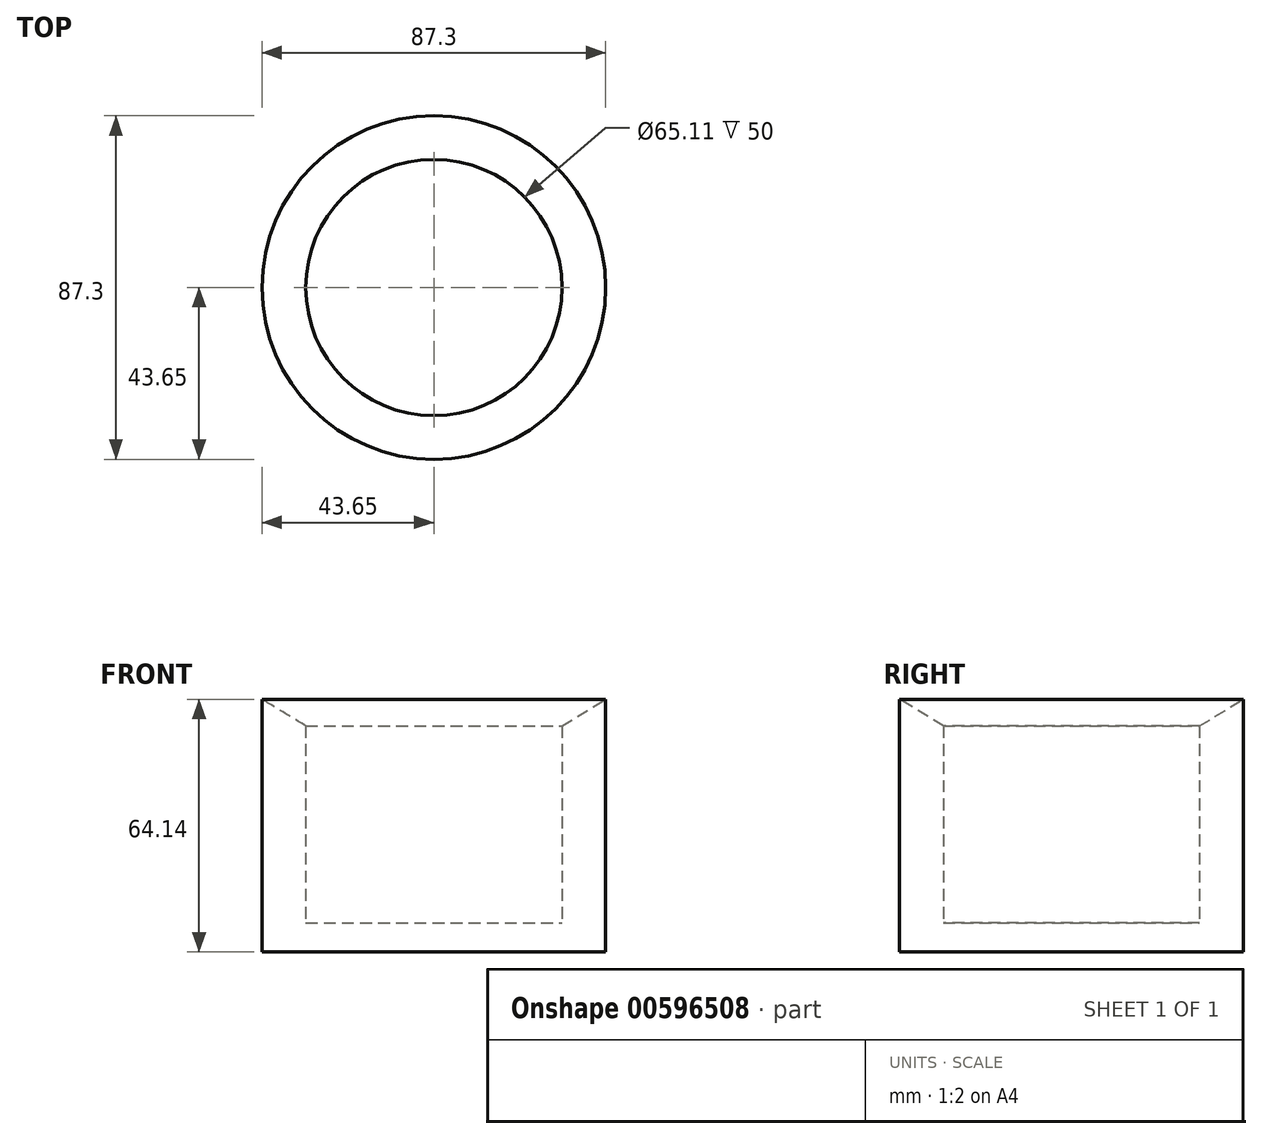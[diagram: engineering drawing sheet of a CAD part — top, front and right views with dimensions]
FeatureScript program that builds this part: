
annotation { "Feature Type Name" : "Feature", "Feature Type Description" : "" }
export const myFeature = defineFeature(function(context is Context, id is Id, definition is map)
    precondition{}
    {
        {
            var Q0;
            Q0=qCreatedBy(makeId("Right.planeOp"),FACE);
            var sketch = newSketch(context, id + "F0", { "sketchPlane" : qUnion([Q0])});
            skLineSegment(sketch, "E0", {"start": v(-43.65, 48.63) * mm, "end": v(-43.65, -15.51) * mm});
            skLineSegment(sketch, "E1", {"start": v(-43.65, -15.51) * mm, "end": v(0, -15.51) * mm});
            skLineSegment(sketch, "E2", {"start": v(0, -15.51) * mm, "end": v(0, -8.12) * mm});
            skLineSegment(sketch, "E3", {"start": v(0, -8.12) * mm, "end": v(-32.56, -8.12) * mm});
            skLineSegment(sketch, "E4", {"start": v(-32.56, -8.12) * mm, "end": v(-32.56, 41.88) * mm});
            skLineSegment(sketch, "E5", {"start": v(-32.56, 41.88) * mm, "end": v(-43.65, 48.63) * mm});
            skSolve(sketch);
        }
        {
            var Q0;
            Q0=makeQuery(id+"F0.imprint","IMPRINT",FACE,{"disambiguationData":[TD([[makeQuery(id+"F0.imprint","IMPRINT",EDGE,{"derivedFrom":sQuery(id+"F0.wireOp",EDGE,"E0")}),1.0]])]});
            var Q1;
            Q1=sQuery(id+"F0.wireOp",EDGE,"E2");
            revolve(context, id + "F1", {"entities" : qUnion([Q0]), "axis" : qUnion([Q1]), "revolveType" : RevolveType.FULL});
        }
    });
